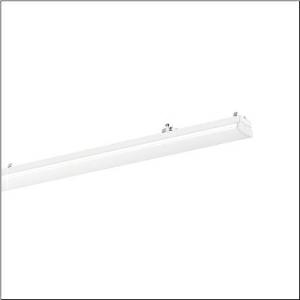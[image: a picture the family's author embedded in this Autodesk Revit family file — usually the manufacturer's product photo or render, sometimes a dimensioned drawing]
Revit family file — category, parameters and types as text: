
# Revit family: licross_r__11_recessed_opal_mo_51tl1ddv4e5g_e7a4
name_source: partatom
category: Lighting Fixtures
units: mm (PartAtom-declared; Revit-internal decimal feet)

## family parameters
Cut with Voids When Loaded = No
Host = Face
Light Source = No
Part Type = Normal
Room Calculation Point = No
Round Connector Dimension = Use Diameter
Shared = No

## types (1)
- --- (1 x LED, 14560 lm, 84.1 W, 4000K)
    Apparent Load = 84 VA
    CIE Flux Codes = 44 73 91 87 100
    Color Rendering = 80
    Color Temperature = 4000K
    Default Elevation = 1800 mm
    Description = Licross® 11 recessed opal MO, luminaire insert, of sheet steel, coil coated, white, length: 2.250mm, width: 76mm, height: 87mm, LED rated luminous flux: 14.560lm, light colour: 840, control gear: DALI 2, with plug, 5-pole, with phase selection, mains connection: 220..240V, AC, 50/60Hz, rated input power: 84W, halogen-free wiring, primary optical cover: cover, of PMMA, light emission: direct with ceiling illumination distribution, primary light characteristic: symmetric, protection rating (complete): IP40, insulation class (complete): insulation class I (protective earthing), certification: CE, ENEC, VDE, UKCA, protection symbol: D if used in an environment without relevant dust loads with corresponding accessories, impact resistance: IK06, permissible ambient temperature for indoor applications: -25..+35°C, corresponds to IFS (International Featured Standards) requirements for safety and quality in the food industry, reducing of maximum allowable ambient temperature of 5°C with ceiling mounting, LABS conformity tested according to VDMA 24364:2018-05, packaging unit: 1 piece
    Height = 83 mm
    Lamp = 1 x LED
    Lamp Light Flux = 14560 lm
    Lamp Power = 84.1 W
    Lamp count = 1
    Length = 2250 mm
    Luminous efficacy = 173 lm/W
    Manufacturer = Siteco
    ModVariant = No
    Model = 51TL1DDV4E5G
    Mounting Place = Ceiling
    Mounting Type = Pendant
    Number of Poles = 1
    OnlyDefault = Yes
    Power Factor = 1
    Product Name = Licross® 11 recessed opal MO
    Product group = luminaire insert
    ProductGroupID = 902
    Protection Class = Protection class I
    Protection Degree = IP 40
    RLX_Detail_Level = 1
    RLX_Emergency_Light_Flux = 0 lm
    RLX_Emergency_Type = 0
    RLX_Emergency_Type_DB = No
    RlxData = <blob elided: 26805 chars, md5=bf851939>
    Socket = socket
    Standby Power = 0 W
    System Light Flux = 14560 lm
    System Power = 84 W
    Type Comments = factory setting: luminous flux: 100 % | dim-lin: 254 | 378 mA
    Type Image = l_1313666.jpg
    URL = http://relux.com
    VarID = @adj_076470
    Voltage = 0 V
    Weight = 0.00 kg
    Width = 76 mm

## geometry (parser evidence)
native form markers: Blend x4, Sweep x13
no freeform markers — native parametric forms only
